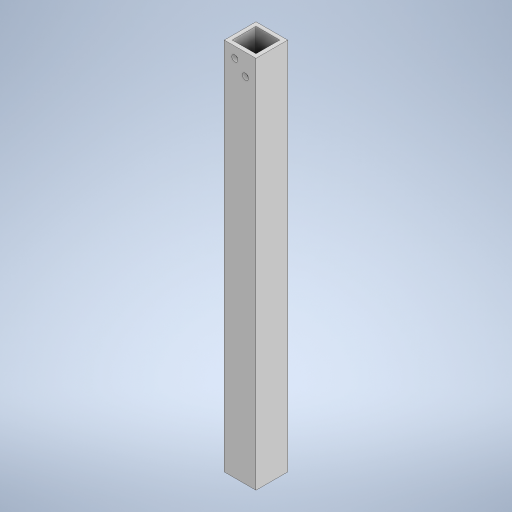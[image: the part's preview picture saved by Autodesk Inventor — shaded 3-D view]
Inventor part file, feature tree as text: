
AUTODESK INVENTOR PART (.ipt)
format: ipt  version: 2023 (Build 270158000, 158)  size: 261,632 bytes
history: native  units: in
note: dims shown in document units (in); Inventor stores cm internally (conversion verified against a paired STEP export)
features: extrude x3, sketch x3
ambient origin geometry x8: Origin, YZ Plane, XZ Plane, XY Plane, X Axis, Y Axis, Z Axis, Center Point
bodies: Solid1 (feature_tree)
feature tree (6):
  extrude  "Extrusion1"  Depth=0.125in
  sketch  "Sketch2"  dims[d2=11.811in d3=0.0in]
  extrude  "Extrusion2"  TaperAngle=0.0deg  [1 undecoded]
  extrude  "Extrusion3"  Depth=0.125in
  sketch  "Sketch1"  dims[d0=1.0in d1=0.125in]
  sketch  "Sketch3"  dims[d4=0.3333in d5=0.191in d6=1.0in d7=0.3333in d8=0.191in d9=0.125in d10=0.0in d11=0.125in d12=0.0in]
note: 1 required parameter value undecoded (feature->parameter linkage not recoverable at this tier; creation-order binding heuristic only, values carry confidence <= 0.55)
